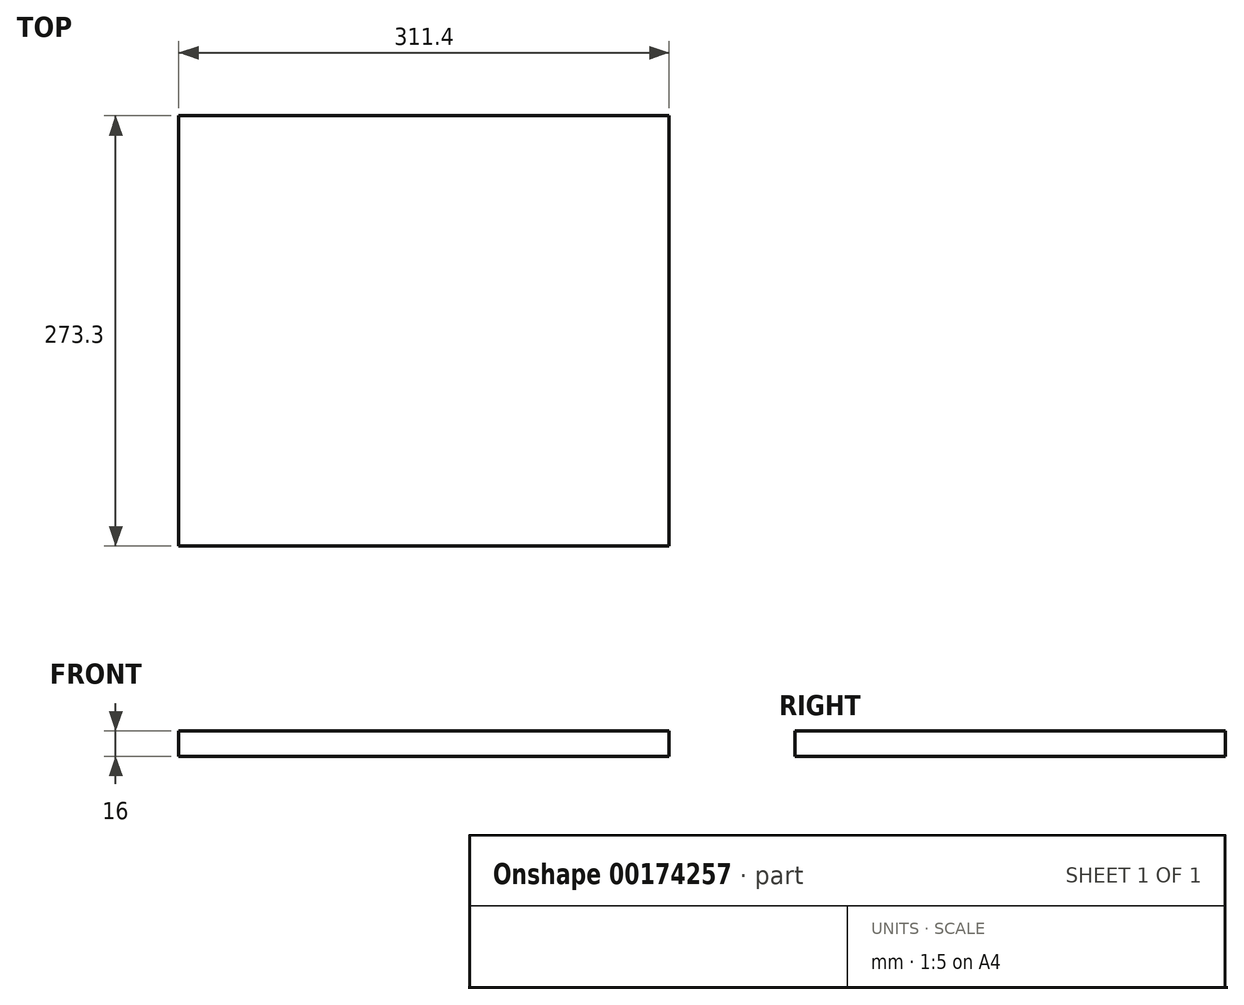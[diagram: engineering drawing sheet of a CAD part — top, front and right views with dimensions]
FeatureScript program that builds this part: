
annotation { "Feature Type Name" : "Feature", "Feature Type Description" : "" }
export const myFeature = defineFeature(function(context is Context, id is Id, definition is map)
    precondition{}
    {
        {
            var Q0;
            Q0=qCreatedBy(makeId("Top.planeOp"),FACE);
            var sketch = newSketch(context, id + "F0", { "sketchPlane" : qUnion([Q0])});
            skLineSegment(sketch, "E0.bottom", {"start": v(-139.7, -120.65) * mm, "end": v(139.7, -120.65) * mm, "construction": true});
            skLineSegment(sketch, "E0.top", {"start": v(-139.7, 120.65) * mm, "end": v(139.7, 120.65) * mm, "construction": true});
            skLineSegment(sketch, "E0.left", {"start": v(-139.7, -120.65) * mm, "end": v(-139.7, 120.65) * mm, "construction": true});
            skLineSegment(sketch, "E0.right", {"start": v(139.7, -120.65) * mm, "end": v(139.7, 120.65) * mm, "construction": true});
            skPoint(sketch, "E0.middle", {"position": v(0, 0) * mm});
            skLineSegment(sketch, "E1.bottom", {"start": v(-155.7, -136.65) * mm, "end": v(155.7, -136.65) * mm});
            skLineSegment(sketch, "E1.top", {"start": v(-155.7, 136.65) * mm, "end": v(155.7, 136.65) * mm});
            skLineSegment(sketch, "E1.left", {"start": v(-155.7, -136.65) * mm, "end": v(-155.7, 136.65) * mm});
            skLineSegment(sketch, "E1.right", {"start": v(155.7, -136.65) * mm, "end": v(155.7, 136.65) * mm});
            skSolve(sketch);
        }
        {
            var Q0;
            Q0=makeQuery(id+"F0.imprint","IMPRINT",FACE,{"disambiguationData":[TD([[makeQuery(id+"F0.imprint","IMPRINT",EDGE,{"derivedFrom":sQuery(id+"F0.wireOp",EDGE,"E1.bottom")}),1.0]])]});
            extrude(context, id + "F1", {"entities" : qUnion([Q0]), "depth" : 16 * mm});
        }
    });
